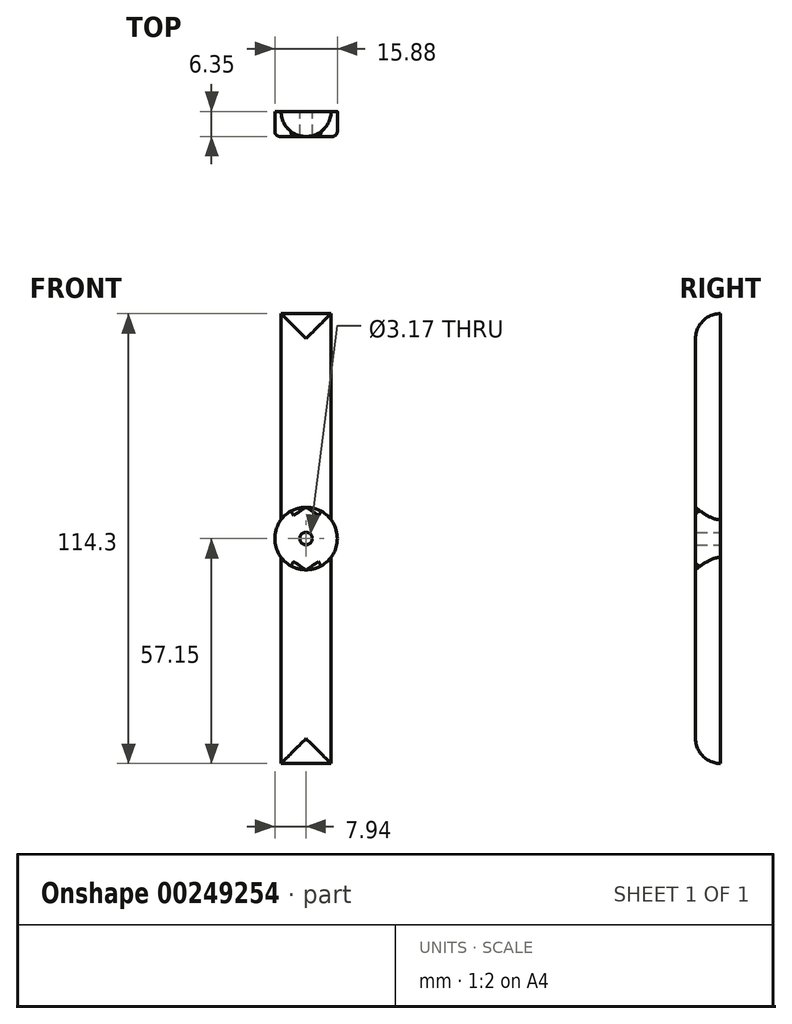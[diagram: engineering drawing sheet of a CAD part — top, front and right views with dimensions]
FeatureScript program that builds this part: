
annotation { "Feature Type Name" : "Feature", "Feature Type Description" : "" }
export const myFeature = defineFeature(function(context is Context, id is Id, definition is map)
    precondition{}
    {
        {
            var Q0;
            Q0=qCreatedBy(makeId("Front.planeOp"),FACE);
            var sketch = newSketch(context, id + "F0", { "sketchPlane" : qUnion([Q0])});
            skLineSegment(sketch, "E0", {"start": v(0, 0) * mm, "end": v(12.7, 0) * mm});
            skLineSegment(sketch, "E1", {"start": v(12.7, 0) * mm, "end": v(12.7, -52.39) * mm});
            skLineSegment(sketch, "E2", {"start": v(12.7, -114.3) * mm, "end": v(0, -114.3) * mm});
            skLineSegment(sketch, "E3", {"start": v(0, -114.3) * mm, "end": v(0, -61.91) * mm});
            skArc(sketch, "E4", {"start": v(0, -52.39) * mm, "mid": v(-1.59, -57.15) * mm, "end": v(0, -61.91) * mm});
            skLineSegment(sketch, "E5.trimOffspring", {"start": v(0, -52.39) * mm, "end": v(0, 0) * mm});
            skLineSegment(sketch, "E6.trimOffspring", {"start": v(12.7, -61.91) * mm, "end": v(12.7, -114.3) * mm});
            skArc(sketch, "E7.trimOffspring", {"start": v(12.7, -61.91) * mm, "mid": v(14.29, -57.15) * mm, "end": v(12.7, -52.39) * mm});
            skCircle(sketch, "E8", {"center": v(6.35, -57.15) * mm, "radius": 1.59 * mm});
            skSolve(sketch);
        }
        {
            var Q0;
            Q0=makeQuery(id+"F0.imprint","IMPRINT",FACE,{"disambiguationData":[TD([[makeQuery(id+"F0.imprint","IMPRINT",EDGE,{"derivedFrom":sQuery(id+"F0.wireOp",EDGE,"E0")}),-1.0]])]});
            extrude(context, id + "F1", {"entities" : qUnion([Q0]), "depth" : 6.35 * mm});
        }
        {
            var Q0;
            Q0=makeQuery(id+"F1.opExtrude","CAP_EDGE",EDGE,{"disambiguationData":[OSD([sQuery(id+"F0.wireOp",EDGE,"E1")])],"isStart":false});
            var Q1;
            Q1=makeQuery(id+"F1.opExtrude","CAP_EDGE",EDGE,{"disambiguationData":[OSD([sQuery(id+"F0.wireOp",EDGE,"E5.trimOffspring")])],"isStart":false});
            var Q2;
            Q2=makeQuery(id+"F1.opExtrude","CAP_EDGE",EDGE,{"disambiguationData":[OSD([sQuery(id+"F0.wireOp",EDGE,"E0")])],"isStart":false});
            var Q3;
            Q3=makeQuery(id+"F1.opExtrude","CAP_EDGE",EDGE,{"disambiguationData":[OSD([sQuery(id+"F0.wireOp",EDGE,"E6.trimOffspring")])],"isStart":false});
            var Q4;
            Q4=makeQuery(id+"F1.opExtrude","CAP_EDGE",EDGE,{"disambiguationData":[OSD([sQuery(id+"F0.wireOp",EDGE,"E3")])],"isStart":false});
            var Q5;
            Q5=makeQuery(id+"F1.opExtrude","CAP_EDGE",EDGE,{"disambiguationData":[OSD([sQuery(id+"F0.wireOp",EDGE,"E2")])],"isStart":false});
            fillet(context, id + "F2", {"entities" : qUnion([Q0, Q1, Q2, Q3, Q4, Q5]), "radius" : 6.35 * mm, "tangentPropagation" : true, "allowEdgeOverflow" : false});
        }
        {
            var Q0;
            Q0=makeQuery(id+"F1.opExtrude","CAP_EDGE",EDGE,{"disambiguationData":[OSD([sQuery(id+"F0.wireOp",EDGE,"E7.trimOffspring")])],"isStart":false});
            var Q1;
            Q1=makeQuery(id+"F1.opExtrude","CAP_EDGE",EDGE,{"disambiguationData":[OSD([sQuery(id+"F0.wireOp",EDGE,"E4")])],"isStart":false});
            fillet(context, id + "F3", {"entities" : qUnion([Q0, Q1]), "radius" : 1.27 * mm, "tangentPropagation" : true, "allowEdgeOverflow" : false});
        }
    });
